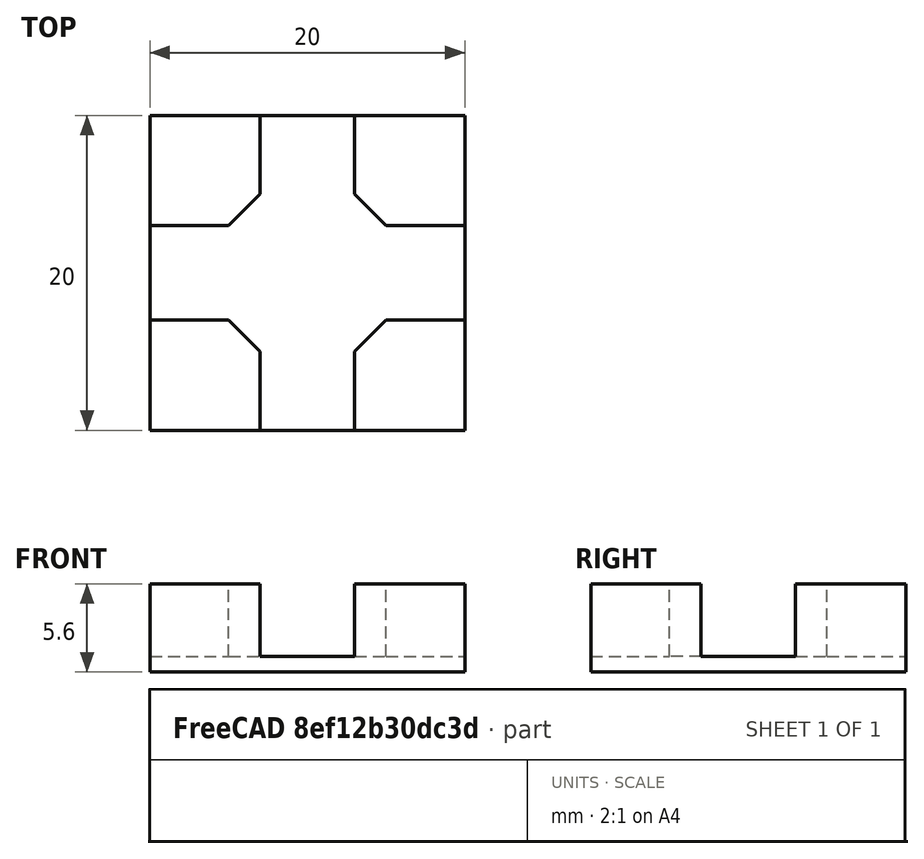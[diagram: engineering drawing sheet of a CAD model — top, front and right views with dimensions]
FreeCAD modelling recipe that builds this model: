
FCSTD DOCUMENT  (FreeCAD 0.16R6700 (Git))
Label: single_pad_base
License: All rights reserved
LicenseURL: http://en.wikipedia.org/wiki/All_rights_reserved
objects: Part::Box×4, Part::MultiFuse×2, Part::Cut×1, Part::Chamfer×1
note: 8 computed .brp shape members not serialized (recipe doc carries the construction recipe); baked Part::Feature solids carry a one-line shape summary decoded from their .brp

FEATURE [Part::Box] Box  label="Cube"
  Height = 4.6
  Length = 20
  Width = 20
FEATURE [Part::Box] Box001  label="Cube001"
  Height = 10
  Length = 6
  Placement = pos=(7,0,0) rot=(0,0,1;0rad)
  Width = 20
FEATURE [Part::Box] Box002  label="Cube002"
  Height = 10
  Length = 20
  Placement = pos=(0,7,0) rot=(0,0,1;0rad)
  Width = 6
FEATURE [Part::MultiFuse] Fusion
  Shapes = -> [Box001,Box002]
FEATURE [Part::Cut] Cut
  Base = -> Box
  Tool = -> Fusion
FEATURE [Part::Chamfer] Chamfer  label="base_button"
  Base = -> Cut
  Edges = 4 edges r=2: [Edge9,Edge24,Edge35,Edge41]
  Placement = pos=(0,0,1) rot=(0,0,1;0rad)
FEATURE [Part::Box] Box003  label="Cube003"
  Height = 1
  Length = 20
  Width = 20
FEATURE [Part::MultiFuse] Fusion001  label="single_pad_base"
  Shapes = -> [Box003,Chamfer]
